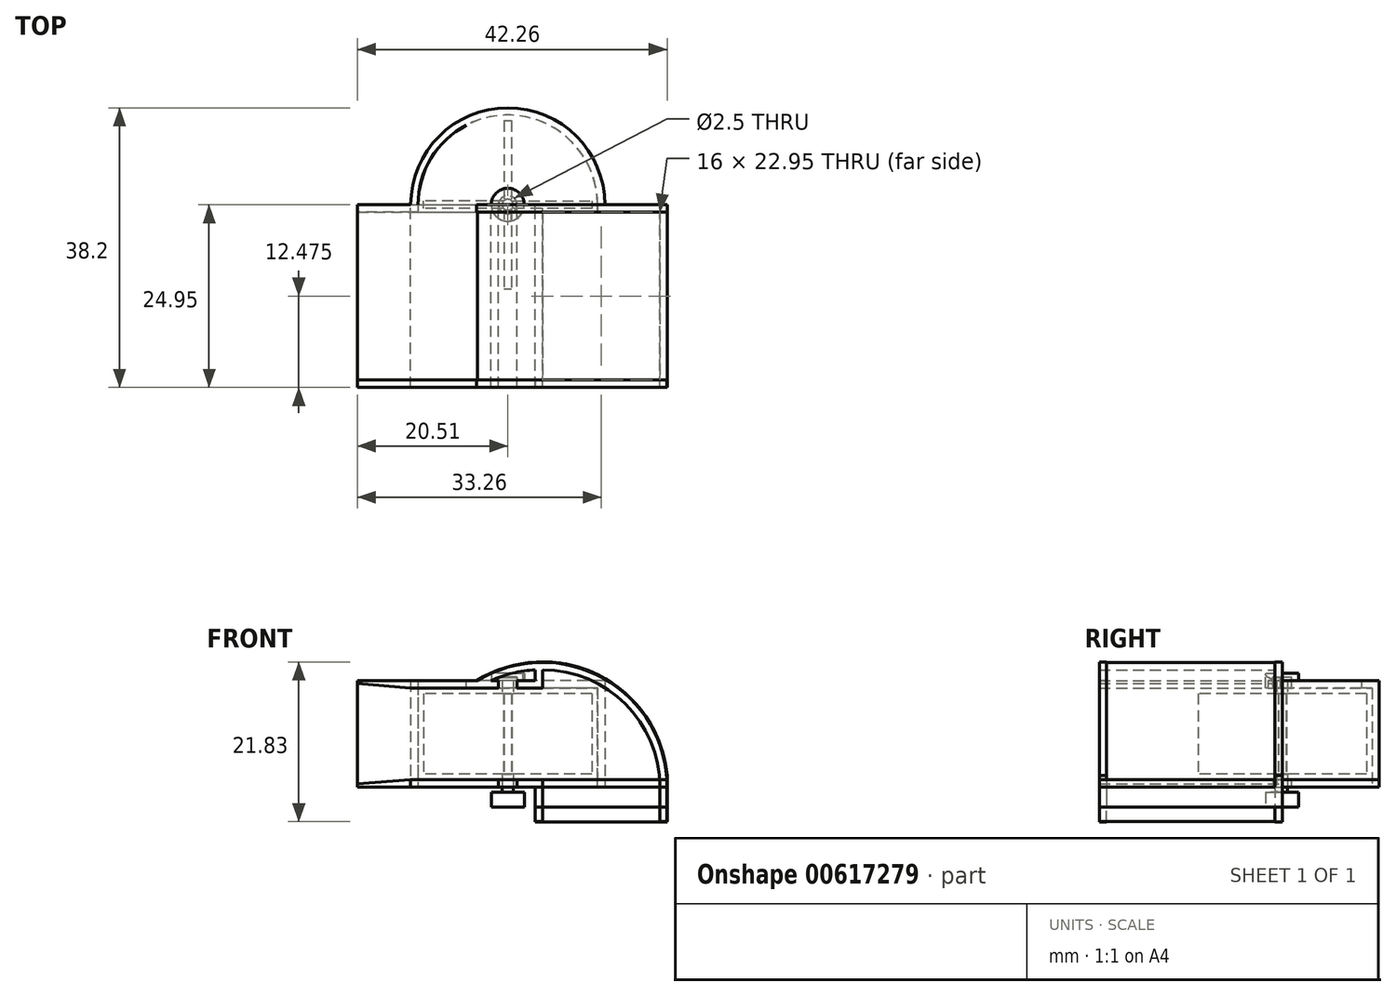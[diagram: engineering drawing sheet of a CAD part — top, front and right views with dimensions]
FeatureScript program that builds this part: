
annotation { "Feature Type Name" : "Feature", "Feature Type Description" : "" }
export const myFeature = defineFeature(function(context is Context, id is Id, definition is map)
    precondition{}
    {
        {
            var Q0;
            Q0=qCreatedBy(makeId("Top.planeOp"),FACE);
            var sketch = newSketch(context, id + "F0", { "sketchPlane" : qUnion([Q0])});
            skLineSegment(sketch, "E0.bottom", {"start": v(0, 0) * mm, "end": v(-20.5, 0) * mm});
            skLineSegment(sketch, "E0.top", {"start": v(0, -24.95) * mm, "end": v(-42.25, -24.95) * mm});
            skLineSegment(sketch, "E0.left", {"start": v(0, 0) * mm, "end": v(0, -24.95) * mm});
            skLineSegment(sketch, "E0.right", {"start": v(-42.25, 0) * mm, "end": v(-42.25, -24.95) * mm});
            skLineSegment(sketch, "E1", {"start": v(-17, -1) * mm, "end": v(-17, -23.95) * mm});
            skLineSegment(sketch, "E2", {"start": v(-35, -23.95) * mm, "end": v(-17, -23.95) * mm});
            skLineSegment(sketch, "E3", {"start": v(-35, -1) * mm, "end": v(-22.5, -1) * mm});
            skLineSegment(sketch, "E4", {"start": v(-17, -23.95) * mm, "end": v(-1, -23.95) * mm});
            skLineSegment(sketch, "E5", {"start": v(-17, -1) * mm, "end": v(-1, -1) * mm});
            skLineSegment(sketch, "E6", {"start": v(-1, -1) * mm, "end": v(-1, -23.95) * mm});
            skLineSegment(sketch, "E7", {"start": v(-35, -1) * mm, "end": v(-42.25, -1) * mm});
            skLineSegment(sketch, "E8", {"start": v(-35, -23.95) * mm, "end": v(-42.25, -23.95) * mm});
            skLineSegment(sketch, "E9", {"start": v(-35, -23.95) * mm, "end": v(-35, -24.95) * mm});
            skLineSegment(sketch, "E10", {"start": v(-35, -1) * mm, "end": v(-35, 0) * mm});
            skLineSegment(sketch, "E11", {"start": v(-35, -23.95) * mm, "end": v(-26, -23.95) * mm});
            skLineSegment(sketch, "E12", {"start": v(-35, -1) * mm, "end": v(-26, -1) * mm});
            skPoint(sketch, "E13", {"position": v(-17, -12.48) * mm});
            skLineSegment(sketch, "E14", {"start": v(-35, -1) * mm, "end": v(-35, -23.95) * mm});
            skPoint(sketch, "E15", {"position": v(-34, 0) * mm});
            skPoint(sketch, "E16", {"position": v(-21.75, 0) * mm});
            skCircle(sketch, "E17", {"center": v(-21.75, 0) * mm, "radius": 0.75 * mm});
            skCircle(sketch, "E18", {"center": v(-21.75, 0) * mm, "radius": 1.25 * mm});
            skArc(sketch, "E19", {"start": v(-9.5, 0) * mm, "mid": v(-21.75, 12.25) * mm, "end": v(-34, 0) * mm});
            skArc(sketch, "E20", {"start": v(-8.5, 0) * mm, "mid": v(-21.75, 13.25) * mm, "end": v(-35, 0) * mm});
            skLineSegment(sketch, "E21.trimOffspring", {"start": v(-23, 0) * mm, "end": v(-42.25, 0) * mm});
            skLineSegment(sketch, "E22.trimOffspring", {"start": v(-21, -1) * mm, "end": v(-17, -1) * mm});
            skLineSegment(sketch, "E23", {"start": v(-34, 0) * mm, "end": v(-34, -1) * mm});
            skLineSegment(sketch, "E24", {"start": v(-9.5, 0) * mm, "end": v(-9.5, -1) * mm});
            skLineSegment(sketch, "E25", {"start": v(-8.5, 0) * mm, "end": v(-8.5, -1) * mm});
            skLineSegment(sketch, "E26", {"start": v(-8.5, -1) * mm, "end": v(-9.5, -1) * mm});
            skSolve(sketch);
        }
        {
            var Q0;
            Q0=qCreatedBy(makeId("Front.planeOp"),FACE);
            var sketch = newSketch(context, id + "F1", { "sketchPlane" : qUnion([Q0])});
            skLineSegment(sketch, "E27", {"start": v(-42.25, 0) * mm, "end": v(-42.25, 0.4) * mm});
            skLineSegment(sketch, "E28", {"start": v(0, 0) * mm, "end": v(0, 0) * mm});
            skLineSegment(sketch, "E29", {"start": v(-1, 0) * mm, "end": v(-1, 0) * mm});
            skLineSegment(sketch, "E30", {"start": v(-1, 0) * mm, "end": v(0, 0) * mm});
            skLineSegment(sketch, "E31", {"start": v(-42.25, 0) * mm, "end": v(-35, 0) * mm});
            skLineSegment(sketch, "E32", {"start": v(-35, 1) * mm, "end": v(-42.25, 0.4) * mm});
            skLineSegment(sketch, "E33", {"start": v(-35, 13.5) * mm, "end": v(-42.25, 14.1) * mm});
            skLineSegment(sketch, "E34", {"start": v(-42.25, 14.1) * mm, "end": v(-42.25, 14.5) * mm});
            skLineSegment(sketch, "E35", {"start": v(-42.25, 14.5) * mm, "end": v(-42.25, 14.1) * mm});
            skLineSegment(sketch, "E36", {"start": v(-35, 0) * mm, "end": v(-26, 0) * mm});
            skLineSegment(sketch, "E37", {"start": v(-25.87, 14.5) * mm, "end": v(-42.25, 14.5) * mm});
            skLineSegment(sketch, "E38", {"start": v(-18, 0) * mm, "end": v(-18, 0) * mm});
            skLineSegment(sketch, "E39", {"start": v(-18, 0) * mm, "end": v(-20.5, 0) * mm});
            skLineSegment(sketch, "E40", {"start": v(-17, 1) * mm, "end": v(-17, 0) * mm});
            skLineSegment(sketch, "E41", {"start": v(-1, 0) * mm, "end": v(-1, -2.75) * mm});
            skLineSegment(sketch, "E42", {"start": v(-18, 0) * mm, "end": v(-18, -2.75) * mm});
            skLineSegment(sketch, "E43", {"start": v(-17, 0) * mm, "end": v(-17, -2.75) * mm});
            skLineSegment(sketch, "E44", {"start": v(-18, -2.75) * mm, "end": v(-17, -2.75) * mm});
            skLineSegment(sketch, "E45", {"start": v(-1, -2.75) * mm, "end": v(0, -2.75) * mm});
            skLineSegment(sketch, "E46", {"start": v(-17, -2.75) * mm, "end": v(-1, -2.75) * mm});
            skLineSegment(sketch, "E47", {"start": v(0, 0) * mm, "end": v(0, -2.75) * mm});
            skArc(sketch, "E48", {"start": v(0, 0) * mm, "mid": v(-5.34, 12.37) * mm, "end": v(-18, 16.97) * mm});
            skArc(sketch, "E49.0", {"start": v(-1, 0) * mm, "mid": v(-6.05, 11.66) * mm, "end": v(-18, 15.97) * mm});
            skLineSegment(sketch, "E50", {"start": v(-35, 13.5) * mm, "end": v(-35, 14.5) * mm});
            skLineSegment(sketch, "E51", {"start": v(-35, 1) * mm, "end": v(-23, 1) * mm});
            skLineSegment(sketch, "E52", {"start": v(-35, 1) * mm, "end": v(-35, 0) * mm});
            skLineSegment(sketch, "E53", {"start": v(-18, 0) * mm, "end": v(-18, 1) * mm});
            skLineSegment(sketch, "E54", {"start": v(-18, 14.5) * mm, "end": v(-20.5, 14.5) * mm});
            skLineSegment(sketch, "E55", {"start": v(-18, 14.5) * mm, "end": v(-18, 15.97) * mm});
            skLineSegment(sketch, "E56", {"start": v(-18, 13.5) * mm, "end": v(-17, 13.5) * mm});
            skLineSegment(sketch, "E57", {"start": v(-17, 13.5) * mm, "end": v(-17, 16) * mm});
            skArc(sketch, "E58", {"start": v(-18, 16.97) * mm, "mid": v(-22.09, 16.22) * mm, "end": v(-25.87, 14.5) * mm});
            skArc(sketch, "E59", {"start": v(-18, 15.97) * mm, "mid": v(-21.1, 15.53) * mm, "end": v(-24.06, 14.5) * mm});
            skLineSegment(sketch, "E60", {"start": v(-18, 13.5) * mm, "end": v(-20.5, 13.5) * mm});
            skPoint(sketch, "E61", {"position": v(-21.75, 13.5) * mm});
            skPoint(sketch, "E62", {"position": v(-34, 13.5) * mm});
            skPoint(sketch, "E63", {"position": v(-21.75, 12.75) * mm});
            skPoint(sketch, "E64", {"position": v(-22.5, 13.5) * mm});
            skPoint(sketch, "E65", {"position": v(-21, 13.5) * mm});
            skLineSegment(sketch, "E66", {"start": v(-22.5, 13.5) * mm, "end": v(-22.5, 1) * mm});
            skLineSegment(sketch, "E67", {"start": v(-21, 13.5) * mm, "end": v(-21, 1) * mm});
            skLineSegment(sketch, "E68", {"start": v(-22.5, 12.75) * mm, "end": v(-33.5, 12.75) * mm});
            skLineSegment(sketch, "E69", {"start": v(-22.5, 13.5) * mm, "end": v(-22.5, 14.5) * mm});
            skLineSegment(sketch, "E70", {"start": v(-21, 13.5) * mm, "end": v(-21, 14.5) * mm});
            skPoint(sketch, "E71", {"position": v(-23, 13.5) * mm});
            skPoint(sketch, "E72", {"position": v(-20.5, 13.5) * mm});
            skLineSegment(sketch, "E73", {"start": v(-23, 13.5) * mm, "end": v(-23, 14.5) * mm});
            skLineSegment(sketch, "E74", {"start": v(-20.5, 13.5) * mm, "end": v(-20.5, 14.5) * mm});
            skLineSegment(sketch, "E75", {"start": v(-21, 12.75) * mm, "end": v(-10, 12.75) * mm});
            skPoint(sketch, "E76", {"position": v(-21.75, 1.75) * mm});
            skLineSegment(sketch, "E77", {"start": v(-22.5, 1.75) * mm, "end": v(-33.5, 1.75) * mm});
            skLineSegment(sketch, "E78", {"start": v(-21, 1.75) * mm, "end": v(-10, 1.75) * mm});
            skLineSegment(sketch, "E79.trimOffspring", {"start": v(-23, 14.5) * mm, "end": v(-25.87, 14.5) * mm});
            skLineSegment(sketch, "E80.trimOffspring", {"start": v(-23, 13.5) * mm, "end": v(-35, 13.5) * mm});
            skLineSegment(sketch, "E81.trimOffspring", {"start": v(-21, 14.5) * mm, "end": v(-22.5, 14.5) * mm});
            skLineSegment(sketch, "E82", {"start": v(-22.5, 1) * mm, "end": v(-22.5, -0.75) * mm});
            skLineSegment(sketch, "E83", {"start": v(-21, 1) * mm, "end": v(-21, -0.75) * mm});
            skLineSegment(sketch, "E84.trimOffspring", {"start": v(-20.5, 1) * mm, "end": v(-17, 1) * mm});
            skLineSegment(sketch, "E85.trimOffspring", {"start": v(-23, 0) * mm, "end": v(-26, 0) * mm});
            skPoint(sketch, "E86", {"position": v(-22.5, -0.75) * mm});
            skLineSegment(sketch, "E87", {"start": v(-22.5, -0.75) * mm, "end": v(-24, -0.75) * mm});
            skLineSegment(sketch, "E88", {"start": v(-24, -0.75) * mm, "end": v(-24, -2.25) * mm});
            skLineSegment(sketch, "E89", {"start": v(-21, -0.75) * mm, "end": v(-19.5, -0.75) * mm});
            skLineSegment(sketch, "E90", {"start": v(-19.5, -2.25) * mm, "end": v(-19.5, -0.75) * mm});
            skLineSegment(sketch, "E91", {"start": v(-21.75, 1.75) * mm, "end": v(-21.75, -2.25) * mm});
            skLineSegment(sketch, "E92", {"start": v(-21.75, 13.5) * mm, "end": v(-21.75, 14.5) * mm});
            skLineSegment(sketch, "E93.trimOffspring", {"start": v(-23, 1) * mm, "end": v(-23, 0) * mm});
            skLineSegment(sketch, "E94.trimOffspring", {"start": v(-20.5, 1) * mm, "end": v(-20.5, 0) * mm});
            skPoint(sketch, "E95", {"position": v(-33.5, 13.5) * mm});
            skLineSegment(sketch, "E96", {"start": v(-33.5, 12.75) * mm, "end": v(-33.5, 1.75) * mm});
            skPoint(sketch, "E97", {"position": v(-10, 12.75) * mm});
            skLineSegment(sketch, "E98", {"start": v(-10, 12.75) * mm, "end": v(-10, 1.75) * mm});
            skLineSegment(sketch, "E99", {"start": v(-34, 13.5) * mm, "end": v(-34, 1) * mm});
            skLineSegment(sketch, "E100", {"start": v(-35, 13.5) * mm, "end": v(-35, 1) * mm});
            skLineSegment(sketch, "E101", {"start": v(-18, -2.75) * mm, "end": v(-24, -2.75) * mm});
            skLineSegment(sketch, "E102", {"start": v(-24, -2.75) * mm, "end": v(-24, -2.25) * mm});
            skLineSegment(sketch, "E103", {"start": v(-19.5, -2.25) * mm, "end": v(-19.5, -2.75) * mm});
            skLineSegment(sketch, "E104", {"start": v(-21.75, -2.25) * mm, "end": v(-21.75, -2.75) * mm});
            skSolve(sketch);
        }
        {
            var Q0;
            Q0=qCreatedBy(makeId("Front.planeOp"),FACE);
            var sketch = newSketch(context, id + "F2", { "sketchPlane" : qUnion([Q0])});
            skLineSegment(sketch, "E105", {"start": v(-42.25, 0) * mm, "end": v(-42.25, 14.5) * mm});
            skLineSegment(sketch, "E106", {"start": v(0, 1.56) * mm, "end": v(0, 0) * mm});
            skLineSegment(sketch, "E107", {"start": v(-42.25, 0) * mm, "end": v(-35, 0) * mm});
            skLineSegment(sketch, "E108", {"start": v(-35, 0) * mm, "end": v(-26, 0) * mm});
            skLineSegment(sketch, "E109", {"start": v(-26, 14.5) * mm, "end": v(-42.25, 14.5) * mm});
            skLineSegment(sketch, "E110", {"start": v(-18, 0) * mm, "end": v(-18, 0) * mm});
            skLineSegment(sketch, "E111", {"start": v(-18, 0) * mm, "end": v(-20.51, 0) * mm});
            skLineSegment(sketch, "E112", {"start": v(-18, 0) * mm, "end": v(-18, -2.76) * mm});
            skLineSegment(sketch, "E113", {"start": v(-18, -2.76) * mm, "end": v(-17, -2.76) * mm});
            skLineSegment(sketch, "E114", {"start": v(-1, -2.76) * mm, "end": v(0, -2.76) * mm});
            skLineSegment(sketch, "E115", {"start": v(-17, -2.76) * mm, "end": v(-1, -2.76) * mm});
            skLineSegment(sketch, "E116", {"start": v(0, 0) * mm, "end": v(0, -2.76) * mm});
            skArc(sketch, "E117", {"start": v(0, 1.56) * mm, "mid": v(-9.4, 15.28) * mm, "end": v(-26, 14.5) * mm});
            skLineSegment(sketch, "E118", {"start": v(-33.96, 1.05) * mm, "end": v(-33.96, 13.55) * mm});
            skLineSegment(sketch, "E119", {"start": v(-9.44, 1.05) * mm, "end": v(-9.44, 13.55) * mm});
            skLineSegment(sketch, "E120", {"start": v(-33.96, 13.55) * mm, "end": v(-23.03, 13.55) * mm});
            skLineSegment(sketch, "E121", {"start": v(-33.96, 1.05) * mm, "end": v(-22.98, 1.05) * mm});
            skLineSegment(sketch, "E122", {"start": v(-22.98, 1.05) * mm, "end": v(-22.98, 0) * mm});
            skLineSegment(sketch, "E123", {"start": v(-20.51, 1.05) * mm, "end": v(-20.51, 0) * mm});
            skLineSegment(sketch, "E124.trimOffspring", {"start": v(-20.51, 1.05) * mm, "end": v(-9.44, 1.05) * mm});
            skLineSegment(sketch, "E125.trimOffspring", {"start": v(-22.98, 0) * mm, "end": v(-26, 0) * mm});
            skLineSegment(sketch, "E126", {"start": v(-23.03, 13.55) * mm, "end": v(-23.03, 14.95) * mm});
            skLineSegment(sketch, "E127", {"start": v(-23.03, 14.95) * mm, "end": v(-20.5, 14.95) * mm});
            skLineSegment(sketch, "E128", {"start": v(-20.5, 14.95) * mm, "end": v(-20.5, 14.5) * mm});
            skLineSegment(sketch, "E129", {"start": v(-20.5, 14.5) * mm, "end": v(-20.5, 13.55) * mm});
            skLineSegment(sketch, "E130.trimOffspring", {"start": v(-20.5, 13.55) * mm, "end": v(-9.44, 13.55) * mm});
            skPoint(sketch, "E131.start.orphan", {"position": v(-9.44, 0) * mm});
            skSolve(sketch);
        }
        {
            var Q0;
            Q0=makeQuery(id+"F2.imprint","IMPRINT",FACE,{"disambiguationData":[TD([[makeQuery(id+"F2.imprint","IMPRINT",EDGE,{"derivedFrom":sQuery(id+"F2.wireOp",EDGE,"E105")}),-1.0]])]});
            cPlane(context, id + "F3", {"entities" : qUnion([Q0]), "cplaneType" : CPlaneType.OFFSET, "offset" : 24.95 * mm, "width" : 150 * mm, "height" : 150 * mm});
        }
        {
            var Q0;
            Q0=qCreatedBy(id+"F3.planeOp",FACE);
            var sketch = newSketch(context, id + "F4", { "sketchPlane" : qUnion([Q0])});
            skLineSegment(sketch, "E132", {"start": v(-42.26, 0) * mm, "end": v(-42.26, 14.5) * mm});
            skLineSegment(sketch, "E133", {"start": v(-0.01, 1.56) * mm, "end": v(-0.01, 0) * mm});
            skLineSegment(sketch, "E134", {"start": v(-42.26, 0) * mm, "end": v(-35.01, 0) * mm});
            skLineSegment(sketch, "E135", {"start": v(-35.01, 0) * mm, "end": v(-26.01, 0) * mm});
            skLineSegment(sketch, "E136", {"start": v(-26.02, 14.5) * mm, "end": v(-42.26, 14.5) * mm});
            skLineSegment(sketch, "E137", {"start": v(-18.01, 0) * mm, "end": v(-18.01, 0) * mm});
            skLineSegment(sketch, "E138", {"start": v(-18.01, 0) * mm, "end": v(-26.01, 0) * mm});
            skLineSegment(sketch, "E139", {"start": v(-18.01, 0) * mm, "end": v(-18.01, -2.76) * mm});
            skLineSegment(sketch, "E140", {"start": v(-18.01, -2.76) * mm, "end": v(-17.01, -2.76) * mm});
            skLineSegment(sketch, "E141", {"start": v(-1.01, -2.76) * mm, "end": v(-0.01, -2.76) * mm});
            skLineSegment(sketch, "E142", {"start": v(-17.01, -2.76) * mm, "end": v(-1.01, -2.76) * mm});
            skLineSegment(sketch, "E143", {"start": v(-0.01, 0) * mm, "end": v(-0.01, -2.76) * mm});
            skArc(sketch, "E144", {"start": v(-0.01, 1.56) * mm, "mid": v(-9.4, 15.28) * mm, "end": v(-26.02, 14.5) * mm});
            skSolve(sketch);
        }
        {
            var Q0;
            Q0 = qSketchRegion(id + "F4", true);
            extrude(context, id + "F5", {"entities" : qUnion([Q0]), "oppositeDirection" : true, "depth" : 1 * mm, "offsetDistance" : 25 * mm});
        }
        {
            var Q0;
            {var subQ0=sQuery(id+"F0.wireOp",EDGE,"E0.left");Q0=makeQuery(id+"F0.imprint","IMPRINT",FACE,{"disambiguationData":[TD([[makeQuery(id+"F0.imprint","IMPRINT",EDGE,{"derivedFrom":subQ0}),-1.0]])]});}
            var Q1;
            Q1=makeQuery(id+"F0.imprint","IMPRINT",FACE,{"disambiguationData":[TD([[makeQuery(id+"F0.imprint","IMPRINT",EDGE,{"derivedFrom":sQuery(id+"F0.wireOp",EDGE,"E1")}),-1.0]])]});
            var Q2;
            {var subQ4=sQuery(id+"F0.wireOp",EDGE,"E3");Q2=makeQuery(id+"F0.imprint","IMPRINT",FACE,{"disambiguationData":[TD([[makeQuery(id+"F0.imprint","IMPRINT",EDGE,{"derivedFrom":subQ4}),1.0]])]});}
            var Q3;
            {var subQ0=sQuery(id+"F0.wireOp",EDGE,"E10");Q3=makeQuery(id+"F0.imprint","IMPRINT",FACE,{"disambiguationData":[TD([[makeQuery(id+"F0.imprint","IMPRINT",EDGE,{"derivedFrom":subQ0}),-1.0]])]});}
            var Q4;
            {var subQ0=sQuery(id+"F0.wireOp",EDGE,"E19");Q4=makeQuery(id+"F0.imprint","IMPRINT",FACE,{"disambiguationData":[TD([[makeQuery(id+"F0.imprint","IMPRINT",EDGE,{"derivedFrom":subQ0}),-1.0]])]});}
            var Q5;
            {var subQ3=sQuery(id+"F0.wireOp",EDGE,"E19");Q5=makeQuery(id+"F0.imprint","IMPRINT",FACE,{"disambiguationData":[TD([[makeQuery(id+"F0.imprint","IMPRINT",EDGE,{"derivedFrom":subQ3}),1.0]])]});}
            var Q6;
            {var subQ0=sQuery(id+"F0.wireOp",EDGE,"E22.trimOffspring");Q6=makeQuery(id+"F0.imprint","IMPRINT",FACE,{"disambiguationData":[TD([[makeQuery(id+"F0.imprint","IMPRINT",EDGE,{"derivedFrom":subQ0}),1.0]])]});}
            var Q7;
            {var subQ0=sQuery(id+"F0.wireOp",EDGE,"E24");Q7=makeQuery(id+"F0.imprint","IMPRINT",FACE,{"disambiguationData":[TD([[makeQuery(id+"F0.imprint","IMPRINT",EDGE,{"derivedFrom":subQ0}),1.0]])]});}
            extrude(context, id + "F6", {"entities" : qUnion([Q0, Q1, Q2, Q3, Q4, Q5, Q6, Q7]), "depth" : 1 * mm, "offsetDistance" : 25 * mm});
        }
        {
            var Q0;
            Q0=makeQuery(id+"F1.imprint","IMPRINT",FACE,{"disambiguationData":[TD([[makeQuery(id+"F1.imprint","IMPRINT",EDGE,{"derivedFrom":sQuery(id+"F1.wireOp",EDGE,"E39")}),-1.0]])]});
            var Q1;
            {var subQ2=sQuery(id+"F1.wireOp",EDGE,"E40");Q1=makeQuery(id+"F1.imprint","IMPRINT",FACE,{"disambiguationData":[TD([[makeQuery(id+"F1.imprint","IMPRINT",EDGE,{"derivedFrom":subQ2}),-1.0]])]});}
            var Q2;
            Q2=makeQuery(id+"F1.imprint","IMPRINT",FACE,{"disambiguationData":[TD([[makeQuery(id+"F1.imprint","IMPRINT",EDGE,{"derivedFrom":sQuery(id+"F1.wireOp",EDGE,"E30")}),-1.0]])]});
            var Q3;
            {var subQ3=sQuery(id+"F1.wireOp",EDGE,"E30");Q3=makeQuery(id+"F1.imprint","IMPRINT",FACE,{"disambiguationData":[TD([[makeQuery(id+"F1.imprint","IMPRINT",EDGE,{"derivedFrom":subQ3}),1.0]])]});}
            var Q4;
            Q4=makeQuery(id+"F1.imprint","IMPRINT",FACE,{"disambiguationData":[TD([[makeQuery(id+"F1.imprint","IMPRINT",EDGE,{"derivedFrom":sQuery(id+"F1.wireOp",EDGE,"E54")}),1.0]])]});
            var Q5;
            {var subQ3=sQuery(id+"F1.wireOp",EDGE,"E50");Q5=makeQuery(id+"F1.imprint","IMPRINT",FACE,{"disambiguationData":[TD([[makeQuery(id+"F1.imprint","IMPRINT",EDGE,{"derivedFrom":subQ3}),-1.0]])]});}
            var Q6;
            Q6=makeQuery(id+"F1.imprint","IMPRINT",FACE,{"disambiguationData":[TD([[makeQuery(id+"F1.imprint","IMPRINT",EDGE,{"derivedFrom":sQuery(id+"F1.wireOp",EDGE,"E33")}),-1.0]])]});
            var Q7;
            Q7=makeQuery(id+"F1.imprint","IMPRINT",FACE,{"disambiguationData":[TD([[makeQuery(id+"F1.imprint","IMPRINT",EDGE,{"derivedFrom":sQuery(id+"F1.wireOp",EDGE,"E31")}),1.0]])]});
            var Q8;
            Q8=makeQuery(id+"F1.imprint","IMPRINT",FACE,{"disambiguationData":[TD([[makeQuery(id+"F1.imprint","IMPRINT",EDGE,{"derivedFrom":sQuery(id+"F1.wireOp",EDGE,"E36")}),1.0]])]});
            extrude(context, id + "F7", {"entities" : qUnion([Q0, Q1, Q2, Q3, Q4, Q5, Q6, Q7, Q8]), "depth" : 24.95 * mm, "offsetDistance" : 25 * mm});
        }
        {
            var Q0;
            Q0=makeQuery(id+"F2.imprint","IMPRINT",FACE,{"disambiguationData":[TD([[makeQuery(id+"F2.imprint","IMPRINT",EDGE,{"derivedFrom":sQuery(id+"F2.wireOp",EDGE,"E105")}),-1.0]])]});
            extrude(context, id + "F8", {"entities" : qUnion([Q0]), "depth" : 1 * mm, "offsetDistance" : 25 * mm});
        }
        {
            var Q0;
            {var subQ0=sQuery(id+"F0.wireOp",EDGE,"E19");Q0=makeQuery(id+"F0.imprint","IMPRINT",FACE,{"disambiguationData":[TD([[makeQuery(id+"F0.imprint","IMPRINT",EDGE,{"derivedFrom":subQ0}),-1.0]])]});}
            var Q1;
            {var subQ0=sQuery(id+"F0.wireOp",EDGE,"E24");Q1=makeQuery(id+"F0.imprint","IMPRINT",FACE,{"disambiguationData":[TD([[makeQuery(id+"F0.imprint","IMPRINT",EDGE,{"derivedFrom":subQ0}),1.0]])]});}
            var Q2;
            {var subQ0=sQuery(id+"F0.wireOp",EDGE,"E10");Q2=makeQuery(id+"F0.imprint","IMPRINT",FACE,{"disambiguationData":[TD([[makeQuery(id+"F0.imprint","IMPRINT",EDGE,{"derivedFrom":subQ0}),-1.0]])]});}
            extrude(context, id + "F9", {"entities" : qUnion([Q0, Q1, Q2]), "depth" : 14.5 * mm, "offsetDistance" : 25 * mm});
        }
        {
            var Q0;
            Q0=qCreatedBy(makeId("Top.planeOp"),FACE);
            cPlane(context, id + "F10", {"entities" : qUnion([Q0]), "cplaneType" : CPlaneType.OFFSET, "offset" : 14.5 * mm, "width" : 150 * mm, "height" : 150 * mm});
        }
        {
            var Q0;
            Q0=qCreatedBy(id+"F10.planeOp",FACE);
            var sketch = newSketch(context, id + "F11", { "sketchPlane" : qUnion([Q0])});
            skLineSegment(sketch, "E145", {"start": v(-34.98, -1) * mm, "end": v(-34.98, 0) * mm});
            skCircle(sketch, "E146", {"center": v(-21.73, 0) * mm, "radius": 1.25 * mm});
            skArc(sketch, "E147", {"start": v(-9.48, 0) * mm, "mid": v(-21.73, 12.26) * mm, "end": v(-33.98, 0) * mm});
            skArc(sketch, "E148", {"start": v(-8.48, 0) * mm, "mid": v(-21.73, 13.26) * mm, "end": v(-34.98, 0) * mm});
            skLineSegment(sketch, "E149", {"start": v(-33.98, 0) * mm, "end": v(-33.98, -1) * mm});
            skLineSegment(sketch, "E150", {"start": v(-9.48, 0) * mm, "end": v(-9.48, -1) * mm});
            skLineSegment(sketch, "E151", {"start": v(-8.48, 0) * mm, "end": v(-8.48, -1) * mm});
            skLineSegment(sketch, "E152", {"start": v(-8.48, -1) * mm, "end": v(-9.48, -1) * mm});
            skLineSegment(sketch, "E153", {"start": v(-19.73, -1) * mm, "end": v(-9.48, -1) * mm});
            skLineSegment(sketch, "E154", {"start": v(-33.98, -1) * mm, "end": v(-23.77, -1) * mm});
            skArc(sketch, "E155", {"start": v(-19.5, 0) * mm, "mid": v(-21.75, 2.25) * mm, "end": v(-24, 0) * mm});
            skLineSegment(sketch, "E156", {"start": v(-19.5, -1) * mm, "end": v(-19.73, -1) * mm});
            skLineSegment(sketch, "E157", {"start": v(-23.77, -1) * mm, "end": v(-24, -1) * mm});
            skLineSegment(sketch, "E158", {"start": v(-24, -1) * mm, "end": v(-24, -1) * mm});
            skArc(sketch, "E159", {"start": v(-24, 0) * mm, "mid": v(-21.75, -2.25) * mm, "end": v(-19.5, 0) * mm});
            skPoint(sketch, "E160.orphan", {"position": v(-20.98, -1) * mm});
            skPoint(sketch, "E161.start.orphan", {"position": v(-22.98, 0) * mm});
            skSolve(sketch);
        }
        {
            var Q0;
            Q0=makeQuery(id+"F9.opExtrude","CAP_FACE",FACE,{"disambiguationData":[OSD([sQuery(id+"F0.wireOp",EDGE,"E10"),sQuery(id+"F0.wireOp",EDGE,"E12"),sQuery(id+"F0.wireOp",EDGE,"E19"),sQuery(id+"F0.wireOp",EDGE,"E20"),sQuery(id+"F0.wireOp",EDGE,"E23"),sQuery(id+"F0.wireOp",EDGE,"E24"),sQuery(id+"F0.wireOp",EDGE,"E25"),sQuery(id+"F0.wireOp",EDGE,"E26")])],"isStart":false});
            var Q1;
            Q1=makeQuery(id+"F11.imprint","IMPRINT",FACE,{"disambiguationData":[TD([[makeQuery(id+"F11.imprint","IMPRINT",EDGE,{"derivedFrom":sQuery(id+"F11.wireOp",EDGE,"E147")}),1.0]])]});
            var Q2;
            Q2=makeQuery(id+"F11.imprint","IMPRINT",FACE,{"disambiguationData":[TD([[makeQuery(id+"F11.imprint","IMPRINT",EDGE,{"derivedFrom":sQuery(id+"F11.wireOp",EDGE,"E146")}),-1.0]])]});
            extrude(context, id + "F12", {"entities" : qUnion([Q0, Q1, Q2]), "operationType" : NewBodyOperationType.ADD, "oppositeDirection" : true, "depth" : 1 * mm, "offsetDistance" : 25 * mm});
        }
        {
            var Q0;
            {var subQ4=sQuery(id+"F11.wireOp",EDGE,"E155");Q0=makeQuery(id+"F11.imprint","IMPRINT",FACE,{"disambiguationData":[TD([[makeQuery(id+"F11.imprint","IMPRINT",EDGE,{"derivedFrom":subQ4}),1.0]])]});}
            extrude(context, id + "F13", {"entities" : qUnion([Q0]), "depth" : 1 * mm, "offsetDistance" : 25 * mm});
        }
        {
            var Q0;
            Q0=qCreatedBy(id+"F10.planeOp",FACE);
            cPlane(context, id + "F14", {"entities" : qUnion([Q0]), "cplaneType" : CPlaneType.OFFSET, "offset" : 1 * mm, "width" : 150 * mm, "height" : 150 * mm});
        }
        {
            var Q0;
            Q0=qCreatedBy(id+"F14.planeOp",FACE);
            var sketch = newSketch(context, id + "F15", { "sketchPlane" : qUnion([Q0])});
            skCircle(sketch, "E162", {"center": v(-21.74, 0) * mm, "radius": 1.25 * mm});
            skArc(sketch, "E163", {"start": v(-19.5, 0) * mm, "mid": v(-21.76, 2.25) * mm, "end": v(-24, 0) * mm});
            skSolve(sketch);
        }
        {
            var Q0;
            Q0=makeQuery(id+"F15.imprint","IMPRINT",FACE,{"disambiguationData":[TD([[makeQuery(id+"F15.imprint","IMPRINT",EDGE,{"derivedFrom":sQuery(id+"F15.wireOp",EDGE,"E162")}),1.0]])]});
            extrude(context, id + "F16", {"entities" : qUnion([Q0]), "operationType" : NewBodyOperationType.ADD, "oppositeDirection" : true, "depth" : 0.5 * mm, "offsetDistance" : 25 * mm});
        }
        {
            var Q0;
            Q0=qCreatedBy(makeId("Top.planeOp"),FACE);
            cPlane(context, id + "F17", {"entities" : qUnion([Q0]), "cplaneType" : CPlaneType.OFFSET, "offset" : 2.75 * mm, "oppositeDirection" : true, "width" : 150 * mm, "height" : 150 * mm});
        }
        {
            var Q0;
            Q0=qCreatedBy(id+"F17.planeOp",FACE);
            var sketch = newSketch(context, id + "F18", { "sketchPlane" : qUnion([Q0])});
            skCircle(sketch, "E164", {"center": v(-21.75, 0) * mm, "radius": 0.75 * mm});
            skCircle(sketch, "E165", {"center": v(-21.75, 0) * mm, "radius": 2.25 * mm});
            skSolve(sketch);
        }
        {
            var Q0;
            Q0=makeQuery(id+"F18.imprint","IMPRINT",FACE,{"disambiguationData":[TD([[makeQuery(id+"F18.imprint","IMPRINT",EDGE,{"derivedFrom":sQuery(id+"F18.wireOp",EDGE,"E164")}),1.0]])]});
            extrude(context, id + "F19", {"entities" : qUnion([Q0]), "depth" : 17.25 * mm, "offsetDistance" : 25 * mm});
        }
        {
            var Q0;
            Q0=makeQuery(id+"F18.imprint","IMPRINT",FACE,{"disambiguationData":[TD([[makeQuery(id+"F18.imprint","IMPRINT",EDGE,{"derivedFrom":sQuery(id+"F18.wireOp",EDGE,"E164")}),-1.0]])]});
            extrude(context, id + "F20", {"entities" : qUnion([Q0]), "operationType" : NewBodyOperationType.ADD, "depth" : 2 * mm, "offsetDistance" : 25 * mm});
        }
        {
            var Q0;
            Q0=qCreatedBy(makeId("Top.planeOp"),FACE);
            cPlane(context, id + "F21", {"entities" : qUnion([Q0]), "cplaneType" : CPlaneType.OFFSET, "offset" : 1.75 * mm, "width" : 150 * mm, "height" : 150 * mm});
        }
        {
            var Q0;
            Q0=qCreatedBy(id+"F21.planeOp",FACE);
            var sketch = newSketch(context, id + "F22", { "sketchPlane" : qUnion([Q0])});
            skLineSegment(sketch, "E166", {"start": v(-20.77, -0.5) * mm, "end": v(-33.26, -0.5) * mm});
            skLineSegment(sketch, "E167", {"start": v(-10.26, 0.5) * mm, "end": v(-10.26, -0.5) * mm});
            skPoint(sketch, "E168.start.orphan", {"position": v(-19.52, 0) * mm});
            skLineSegment(sketch, "E169", {"start": v(-22.26, 11.5) * mm, "end": v(-22.26, -11.5) * mm});
            skLineSegment(sketch, "E170", {"start": v(-21.26, 11.5) * mm, "end": v(-21.26, -11.5) * mm});
            skLineSegment(sketch, "E171", {"start": v(-21.26, 0.5) * mm, "end": v(-10.26, 0.5) * mm});
            skLineSegment(sketch, "E172", {"start": v(-10.26, -0.5) * mm, "end": v(-20.77, -0.5) * mm});
            skPoint(sketch, "E173.start.orphan", {"position": v(-21.76, 0) * mm});
            skLineSegment(sketch, "E174", {"start": v(-21.26, 0.5) * mm, "end": v(-33.26, 0.5) * mm});
            skLineSegment(sketch, "E175", {"start": v(-22.26, 0.5) * mm, "end": v(-21.26, -0.5) * mm});
            skLineSegment(sketch, "E176", {"start": v(-21.26, -0.5) * mm, "end": v(-21.26, 0.5) * mm});
            skLineSegment(sketch, "E177", {"start": v(-21.26, 0.5) * mm, "end": v(-22.26, -0.5) * mm});
            skLineSegment(sketch, "E178", {"start": v(-33.26, -0.5) * mm, "end": v(-33.26, 0.5) * mm});
            skLineSegment(sketch, "E179", {"start": v(-22.26, 11.5) * mm, "end": v(-21.26, 11.5) * mm});
            skLineSegment(sketch, "E180", {"start": v(-22.26, -11.5) * mm, "end": v(-21.26, -11.5) * mm});
            skSolve(sketch);
        }
        {
            var Q0;
            Q0 = qSketchRegion(id + "F22", true);
            extrude(context, id + "F23", {"entities" : qUnion([Q0]), "operationType" : NewBodyOperationType.ADD, "depth" : 11 * mm, "offsetDistance" : 25 * mm});
        }
        {
            var Q0;
            Q0=makeQuery(id+"F8.opExtrude","SWEPT_FACE",FACE,{"disambiguationData":[OSD([sQuery(id+"F2.wireOp",EDGE,"E113"),sQuery(id+"F2.wireOp",EDGE,"E114"),sQuery(id+"F2.wireOp",EDGE,"E115")])]});
            var Q1;
            Q1=makeQuery(id+"F7.opExtrude","SWEPT_FACE",FACE,{"disambiguationData":[OSD([sQuery(id+"F1.wireOp",EDGE,"E44")])]});
            var Q2;
            Q2=makeQuery(id+"F7.opExtrude","SWEPT_FACE",FACE,{"disambiguationData":[OSD([sQuery(id+"F1.wireOp",EDGE,"E45")])]});
            var Q3;
            Q3=makeQuery(id+"F5.opExtrude","SWEPT_FACE",FACE,{"disambiguationData":[OSD([sQuery(id+"F4.wireOp",EDGE,"E140"),sQuery(id+"F4.wireOp",EDGE,"E141"),sQuery(id+"F4.wireOp",EDGE,"E142")])]});
            extrude(context, id + "F24", {"entities" : qUnion([Q0, Q1, Q2, Q3]), "depth" : 2 * mm, "offsetDistance" : 25 * mm});
        }
    });
